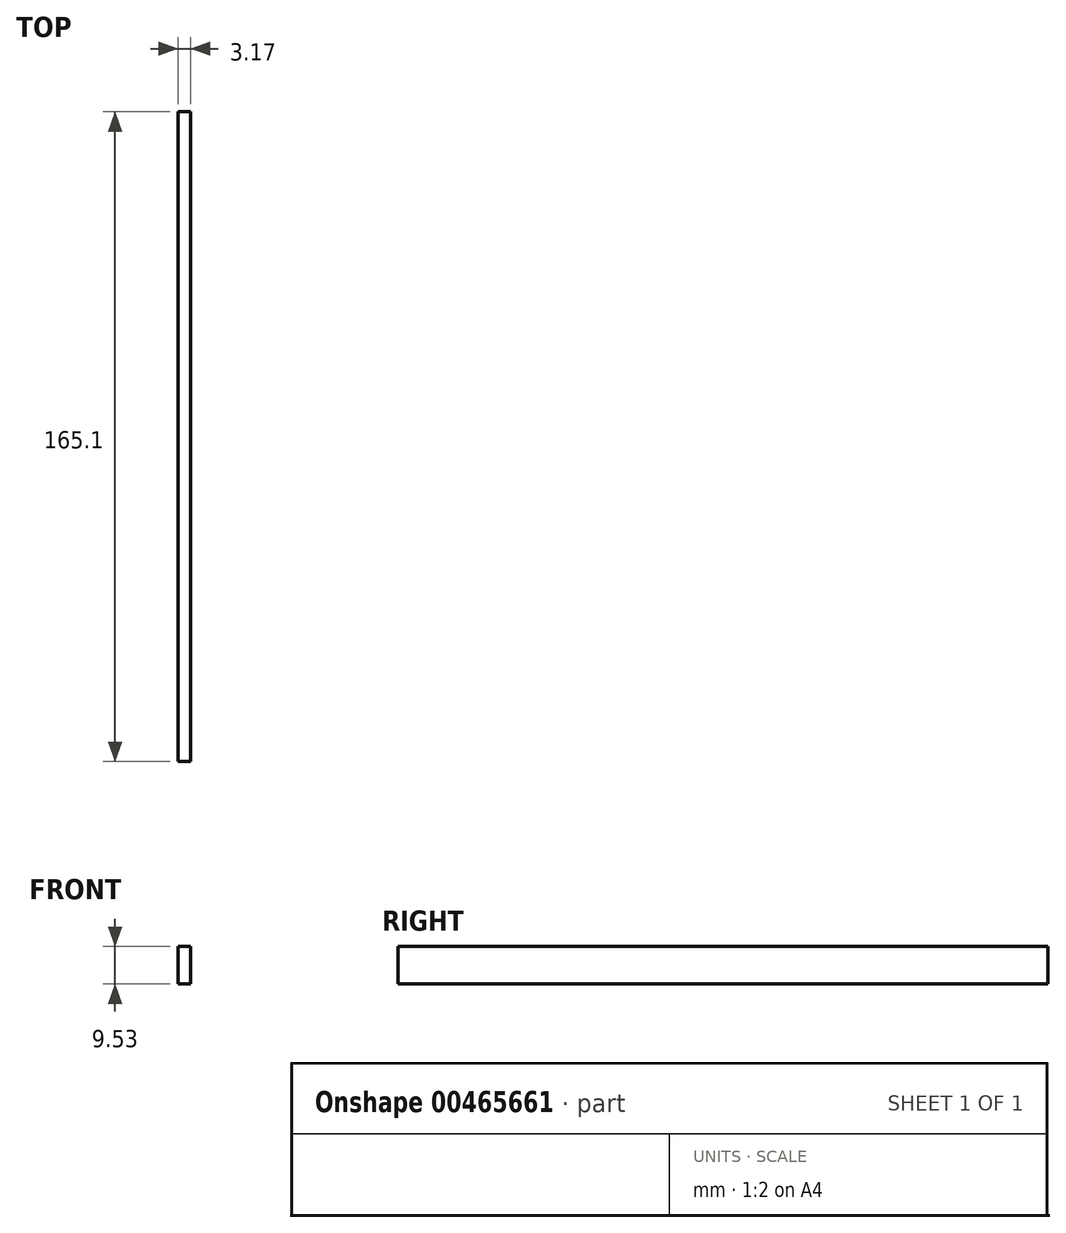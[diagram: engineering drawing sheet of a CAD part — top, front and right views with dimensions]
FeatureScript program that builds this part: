
annotation { "Feature Type Name" : "Feature", "Feature Type Description" : "" }
export const myFeature = defineFeature(function(context is Context, id is Id, definition is map)
    precondition{}
    {
        {
            var Q0;
            Q0=qCreatedBy(makeId("Right.planeOp"),FACE);
            var sketch = newSketch(context, id + "F0", { "sketchPlane" : qUnion([Q0])});
            skLineSegment(sketch, "E0.bottom", {"start": v(0, 0) * mm, "end": v(165.1, 0) * mm});
            skLineSegment(sketch, "E0.top", {"start": v(0, 9.53) * mm, "end": v(165.1, 9.53) * mm});
            skLineSegment(sketch, "E0.left", {"start": v(0, 0) * mm, "end": v(0, 9.53) * mm});
            skLineSegment(sketch, "E0.right", {"start": v(165.1, 0) * mm, "end": v(165.1, 9.53) * mm});
            skSolve(sketch);
        }
        {
            var Q0;
            Q0=qSketchRegion(id+"F0",true);
            extrude(context, id + "F1", {"entities" : qUnion([Q0]), "depth" : 3.17 * mm});
        }
    });
